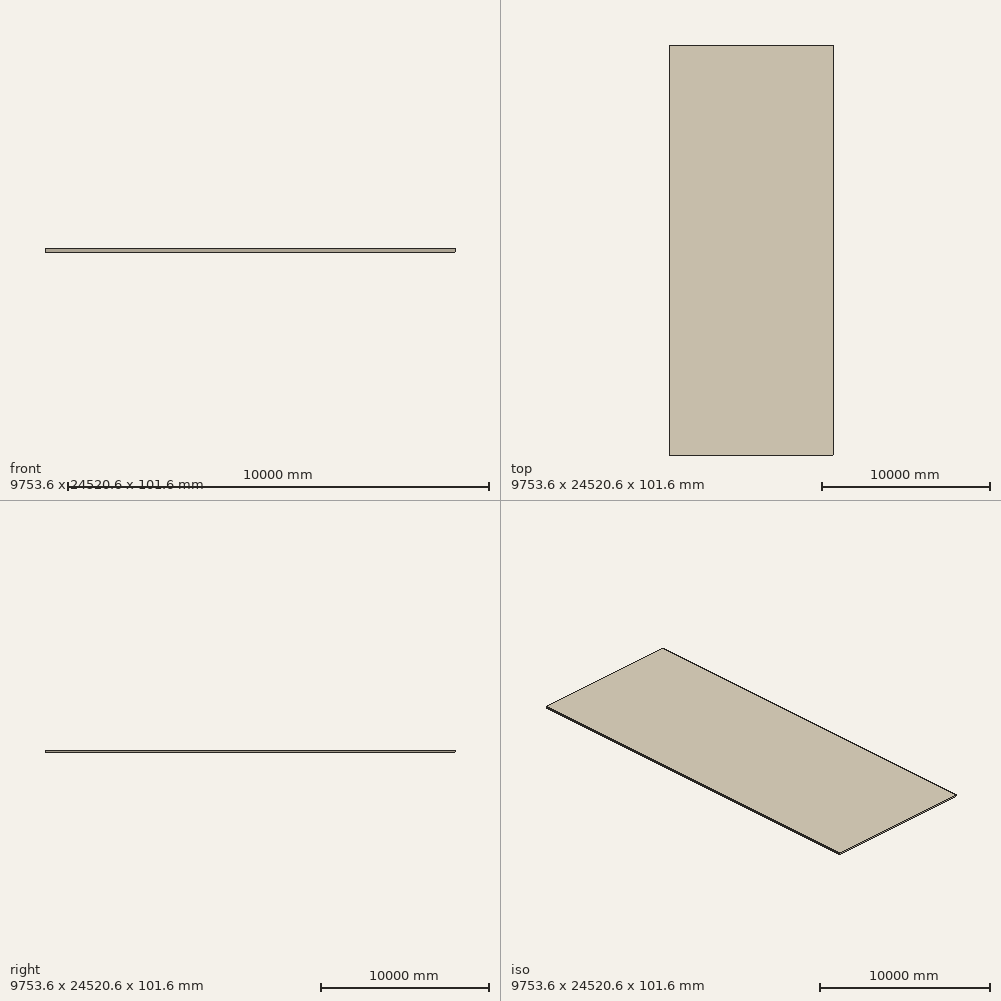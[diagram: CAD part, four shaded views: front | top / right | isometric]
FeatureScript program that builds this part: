
annotation { "Feature Type Name" : "Feature", "Feature Type Description" : "" }
export const myFeature = defineFeature(function(context is Context, id is Id, definition is map)
    precondition{}
    {
        {
            var Q0;
            Q0=qCreatedBy(makeId("Top.planeOp"),FACE);
            var sketch = newSketch(context, id + "F0", { "sketchPlane" : qUnion([Q0])});
            skLineSegment(sketch, "E0.bottom", {"start": v(-4876.8, -12260.28) * mm, "end": v(4876.8, -12260.28) * mm});
            skLineSegment(sketch, "E0.top", {"start": v(-4876.8, 12260.28) * mm, "end": v(4876.8, 12260.28) * mm});
            skLineSegment(sketch, "E0.left", {"start": v(-4876.8, -12260.28) * mm, "end": v(-4876.8, 12260.28) * mm});
            skLineSegment(sketch, "E0.right", {"start": v(4876.8, -12260.28) * mm, "end": v(4876.8, 12260.28) * mm});
            skPoint(sketch, "E0.middle", {"position": v(0, 0) * mm});
            skSolve(sketch);
        }
        {
            var Q0;
            Q0=makeQuery(id+"F0.imprint","IMPRINT",FACE,{"disambiguationData":[TD([[makeQuery(id+"F0.imprint","IMPRINT",EDGE,{"derivedFrom":sQuery(id+"F0.wireOp",EDGE,"E0.bottom")}),1.0]])]});
            extrude(context, id + "F1", {"entities" : qUnion([Q0]), "depth" : 101.6 * mm});
        }
    });
